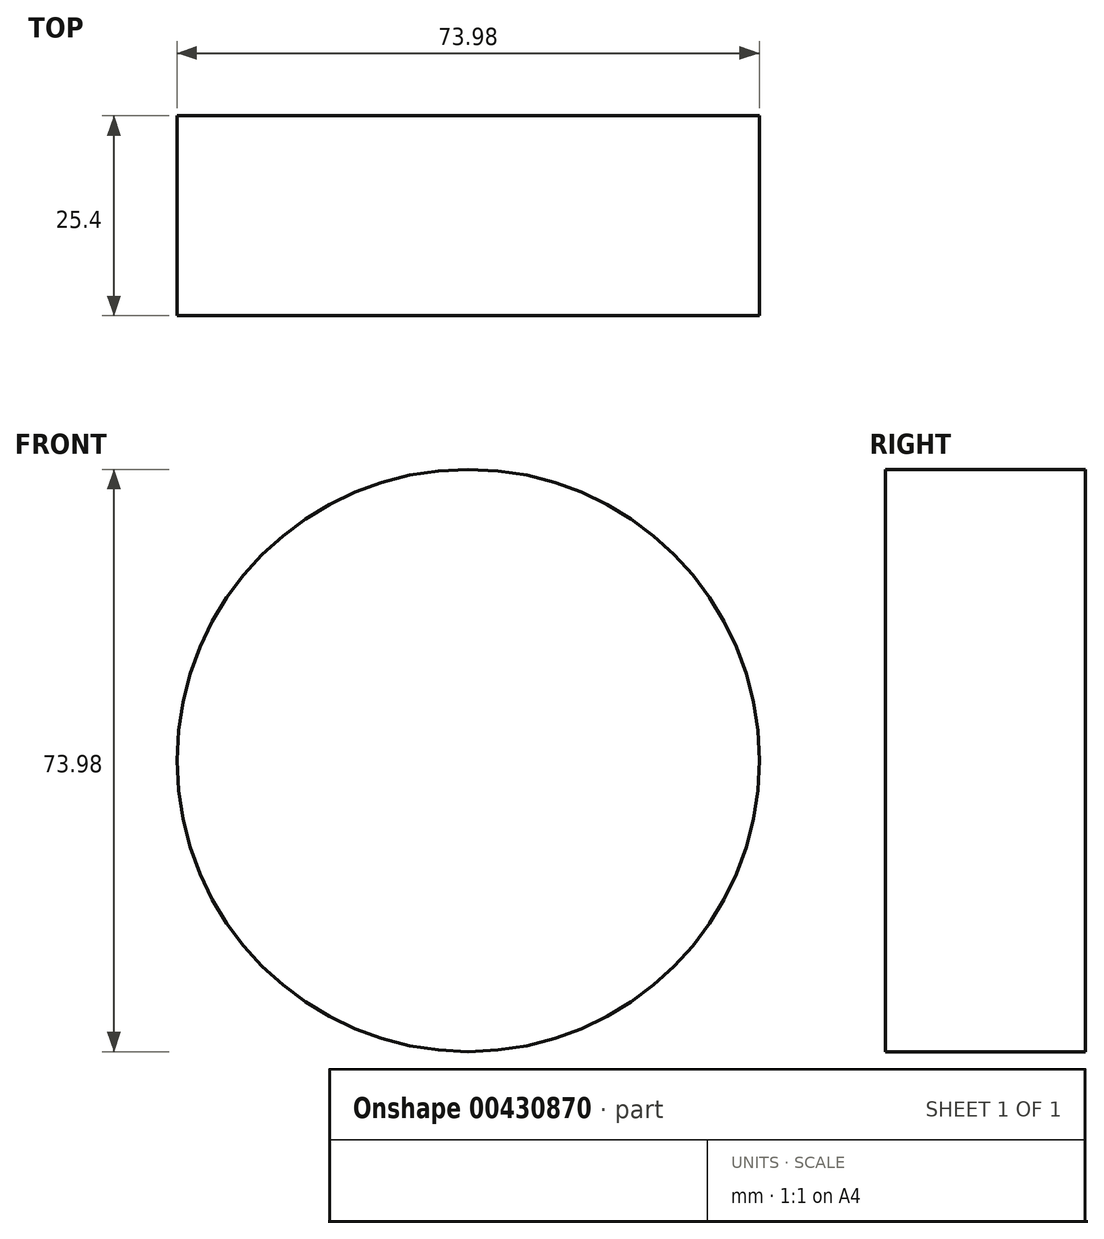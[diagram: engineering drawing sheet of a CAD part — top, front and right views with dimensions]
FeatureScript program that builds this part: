
annotation { "Feature Type Name" : "Feature", "Feature Type Description" : "" }
export const myFeature = defineFeature(function(context is Context, id is Id, definition is map)
    precondition{}
    {
        {
            var Q0;
            Q0=qCreatedBy(makeId("Front.planeOp"),FACE);
            var sketch = newSketch(context, id + "F0", { "sketchPlane" : qUnion([Q0])});
            skLineSegment(sketch, "E0", {"start": v(-33.38, -27.77) * mm, "end": v(0, 0) * mm});
            skCircle(sketch, "E1", {"center": v(-33.38, -27.77) * mm, "radius": 36.99 * mm});
            skSolve(sketch);
        }
        {
            var Q0;
            Q0=sQuery(id+"F0.wireOp",EDGE,"E1");
            extrude(context, id + "F1", {"bodyType" : ToolBodyType.SURFACE, "surfaceEntities" : qUnion([Q0]), "depth" : 25.4 * mm});
        }
        {
            var Q0;
            Q0=qCreatedBy(makeId("Top.planeOp"),FACE);
            var sketch = newSketch(context, id + "F2", { "sketchPlane" : qUnion([Q0])});
            skLineSegment(sketch, "E2", {"start": v(5.73, -24.7) * mm, "end": v(34.18, -68.32) * mm});
            skSolve(sketch);
        }
    });
